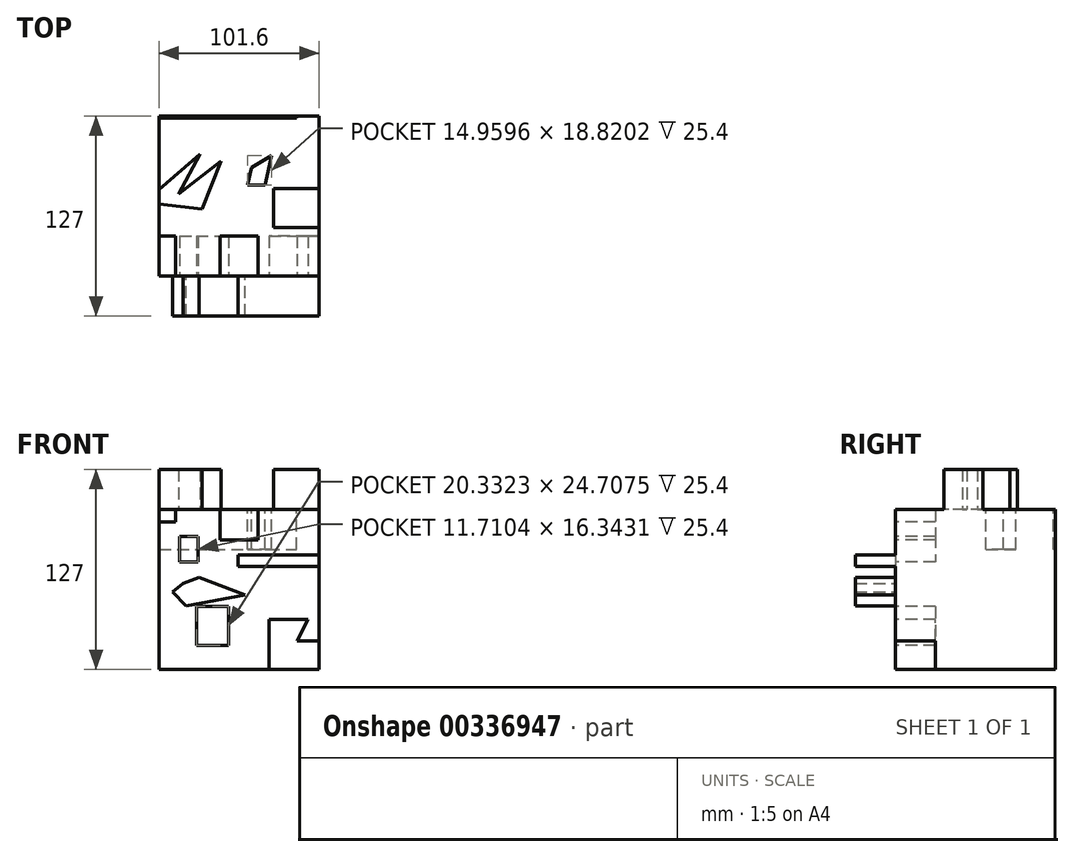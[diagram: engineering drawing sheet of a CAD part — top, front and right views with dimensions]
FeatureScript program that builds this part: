
annotation { "Feature Type Name" : "Feature", "Feature Type Description" : "" }
export const myFeature = defineFeature(function(context is Context, id is Id, definition is map)
    precondition{}
    {
        {
            var Q0;
            Q0=qCreatedBy(makeId("Front.planeOp"),FACE);
            var sketch = newSketch(context, id + "F0", { "sketchPlane" : qUnion([Q0])});
            skLineSegment(sketch, "E0.bottom", {"start": v(-49.93, 54.86) * mm, "end": v(51.67, 54.86) * mm});
            skLineSegment(sketch, "E0.top", {"start": v(-49.93, -46.74) * mm, "end": v(51.67, -46.74) * mm});
            skLineSegment(sketch, "E0.left", {"start": v(-49.93, 54.86) * mm, "end": v(-49.93, -46.74) * mm});
            skLineSegment(sketch, "E0.right", {"start": v(51.67, 54.86) * mm, "end": v(51.67, -46.74) * mm});
            skSolve(sketch);
        }
        {
            var Q0;
            Q0=makeQuery(id+"F0.imprint","IMPRINT",FACE,{"disambiguationData":[TD([[makeQuery(id+"F0.imprint","IMPRINT",EDGE,{"derivedFrom":sQuery(id+"F0.wireOp",EDGE,"E0.bottom")}),-1.0]])]});
            extrude(context, id + "F1", {"entities" : qUnion([Q0]), "oppositeDirection" : true, "depth" : 101.6 * mm});
        }
        {
            var Q0;
            Q0=makeQuery(id+"F1.opExtrude","CAP_FACE",FACE,{"disambiguationData":[OSD([sQuery(id+"F0.wireOp",EDGE,"E0.bottom"),sQuery(id+"F0.wireOp",EDGE,"E0.top"),sQuery(id+"F0.wireOp",EDGE,"E0.left"),sQuery(id+"F0.wireOp",EDGE,"E0.right")])],"isStart":true});
            var sketch = newSketch(context, id + "F2", { "sketchPlane" : qUnion([Q0])});
            skLineSegment(sketch, "E1.bottom", {"start": v(-49.93, 54.86) * mm, "end": v(-39.47, 54.86) * mm});
            skLineSegment(sketch, "E1.top", {"start": v(-49.93, 47.1) * mm, "end": v(-39.47, 47.1) * mm});
            skLineSegment(sketch, "E1.left", {"start": v(-49.93, 54.86) * mm, "end": v(-49.93, 47.1) * mm});
            skLineSegment(sketch, "E1.right", {"start": v(-39.47, 54.86) * mm, "end": v(-39.47, 47.1) * mm});
            skLineSegment(sketch, "E2.bottom", {"start": v(-36.77, 37.84) * mm, "end": v(-25.06, 37.84) * mm});
            skLineSegment(sketch, "E2.top", {"start": v(-36.77, 21.5) * mm, "end": v(-25.06, 21.5) * mm});
            skLineSegment(sketch, "E2.left", {"start": v(-36.77, 37.84) * mm, "end": v(-36.77, 21.5) * mm});
            skLineSegment(sketch, "E2.right", {"start": v(-25.06, 37.84) * mm, "end": v(-25.06, 21.5) * mm});
            skLineSegment(sketch, "E3", {"start": v(51.67, -28.57) * mm, "end": v(37.6, -28.57) * mm});
            skLineSegment(sketch, "E4", {"start": v(37.6, -28.57) * mm, "end": v(44.69, -14.92) * mm});
            skLineSegment(sketch, "E5", {"start": v(44.69, -14.92) * mm, "end": v(19.98, -14.92) * mm});
            skLineSegment(sketch, "E6", {"start": v(19.98, -14.92) * mm, "end": v(19.98, -46.74) * mm});
            skLineSegment(sketch, "E7", {"start": v(19.98, -46.74) * mm, "end": v(51.67, -46.74) * mm});
            skLineSegment(sketch, "E8", {"start": v(51.67, -46.74) * mm, "end": v(51.67, -28.57) * mm});
            skLineSegment(sketch, "E9.bottom", {"start": v(12.9, 54.86) * mm, "end": v(-11.3, 54.86) * mm});
            skLineSegment(sketch, "E9.top", {"start": v(12.9, 35.4) * mm, "end": v(-11.3, 35.4) * mm});
            skLineSegment(sketch, "E9.left", {"start": v(12.9, 54.86) * mm, "end": v(12.9, 35.4) * mm});
            skLineSegment(sketch, "E9.right", {"start": v(-11.3, 54.86) * mm, "end": v(-11.3, 35.4) * mm});
            skLineSegment(sketch, "E10.bottom", {"start": v(-26.22, -6.82) * mm, "end": v(-5.89, -6.82) * mm});
            skLineSegment(sketch, "E10.top", {"start": v(-26.22, -31.53) * mm, "end": v(-5.89, -31.53) * mm});
            skLineSegment(sketch, "E10.left", {"start": v(-26.22, -6.82) * mm, "end": v(-26.22, -31.53) * mm});
            skLineSegment(sketch, "E10.right", {"start": v(-5.89, -6.82) * mm, "end": v(-5.89, -31.53) * mm});
            skLineSegment(sketch, "E11.bottom", {"start": v(51.67, 26.13) * mm, "end": v(0.16, 26.13) * mm});
            skLineSegment(sketch, "E11.top", {"start": v(51.67, 18.53) * mm, "end": v(0.16, 18.53) * mm});
            skLineSegment(sketch, "E11.left", {"start": v(51.67, 26.13) * mm, "end": v(51.67, 18.53) * mm});
            skLineSegment(sketch, "E11.right", {"start": v(0.16, 26.13) * mm, "end": v(0.16, 18.53) * mm});
            skLineSegment(sketch, "E12", {"start": v(-34.84, 7.98) * mm, "end": v(-24.42, 11.84) * mm});
            skLineSegment(sketch, "E13", {"start": v(-24.42, 11.84) * mm, "end": v(4.8, 0.52) * mm});
            skLineSegment(sketch, "E14", {"start": v(4.8, 0.52) * mm, "end": v(-32.91, -6.43) * mm});
            skLineSegment(sketch, "E15", {"start": v(-32.91, -6.43) * mm, "end": v(-41.28, 2.45) * mm});
            skLineSegment(sketch, "E16", {"start": v(-41.28, 2.45) * mm, "end": v(-34.84, 7.98) * mm});
            skSolve(sketch);
        }
        {
            var Q0;
            Q0=makeQuery(id+"F2.imprint","IMPRINT",FACE,{"disambiguationData":[TD([[makeQuery(id+"F2.imprint","IMPRINT",EDGE,{"derivedFrom":sQuery(id+"F2.wireOp",EDGE,"E1.bottom")}),-1.0]])]});
            var Q1;
            Q1=makeQuery(id+"F2.imprint","IMPRINT",FACE,{"disambiguationData":[TD([[makeQuery(id+"F2.imprint","IMPRINT",EDGE,{"derivedFrom":sQuery(id+"F2.wireOp",EDGE,"E9.bottom")}),-1.0]])]});
            var Q2;
            Q2=makeQuery(id+"F2.imprint","IMPRINT",FACE,{"disambiguationData":[TD([[makeQuery(id+"F2.imprint","IMPRINT",EDGE,{"derivedFrom":sQuery(id+"F2.wireOp",EDGE,"E2.bottom")}),-1.0]])]});
            var Q3;
            Q3=makeQuery(id+"F2.imprint","IMPRINT",FACE,{"disambiguationData":[TD([[makeQuery(id+"F2.imprint","IMPRINT",EDGE,{"derivedFrom":sQuery(id+"F2.wireOp",EDGE,"E10.bottom")}),-1.0]])]});
            var Q4;
            Q4=makeQuery(id+"F2.imprint","IMPRINT",FACE,{"disambiguationData":[TD([[makeQuery(id+"F2.imprint","IMPRINT",EDGE,{"derivedFrom":sQuery(id+"F2.wireOp",EDGE,"E3")}),1.0]])]});
            extrude(context, id + "F3", {"entities" : qUnion([Q0, Q1, Q2, Q3, Q4]), "operationType" : NewBodyOperationType.REMOVE, "oppositeDirection" : true, "depth" : 25.4 * mm});
        }
        {
            var Q0;
            Q0=makeQuery(id+"F2.imprint","IMPRINT",FACE,{"disambiguationData":[TD([[makeQuery(id+"F2.imprint","IMPRINT",EDGE,{"derivedFrom":sQuery(id+"F2.wireOp",EDGE,"E12")}),-1.0]])]});
            var Q1;
            Q1=makeQuery(id+"F2.imprint","IMPRINT",FACE,{"disambiguationData":[TD([[makeQuery(id+"F2.imprint","IMPRINT",EDGE,{"derivedFrom":sQuery(id+"F2.wireOp",EDGE,"E11.bottom")}),1.0]])]});
            extrude(context, id + "F4", {"entities" : qUnion([Q0, Q1]), "operationType" : NewBodyOperationType.ADD, "depth" : 25.4 * mm});
        }
        {
            var Q0;
            Q0=makeQuery(id+"F1.opExtrude","SWEPT_FACE",FACE,{"disambiguationData":[OSD([sQuery(id+"F0.wireOp",EDGE,"E0.bottom")])]});
            var sketch = newSketch(context, id + "F5", { "sketchPlane" : qUnion([Q0])});
            skLineSegment(sketch, "E17.bottom", {"start": v(51.67, 55.55) * mm, "end": v(22.83, 55.55) * mm});
            skLineSegment(sketch, "E17.top", {"start": v(51.67, 30.78) * mm, "end": v(22.83, 30.78) * mm});
            skLineSegment(sketch, "E17.left", {"start": v(51.67, 55.55) * mm, "end": v(51.67, 30.78) * mm});
            skLineSegment(sketch, "E17.right", {"start": v(22.83, 55.55) * mm, "end": v(22.83, 30.78) * mm});
            skLineSegment(sketch, "E18.bottom", {"start": v(-49.93, 100.43) * mm, "end": v(37.3, 100.43) * mm});
            skLineSegment(sketch, "E18.top", {"start": v(-49.93, 101.6) * mm, "end": v(37.3, 101.6) * mm});
            skLineSegment(sketch, "E18.left", {"start": v(-49.93, 100.43) * mm, "end": v(-49.93, 101.6) * mm});
            skLineSegment(sketch, "E18.right", {"start": v(37.3, 100.43) * mm, "end": v(37.3, 101.6) * mm});
            skLineSegment(sketch, "E19", {"start": v(-49.93, 55.06) * mm, "end": v(-23.98, 77.42) * mm});
            skLineSegment(sketch, "E20", {"start": v(-23.98, 77.42) * mm, "end": v(-37.5, 52.17) * mm});
            skLineSegment(sketch, "E21", {"start": v(-37.5, 52.17) * mm, "end": v(-10.47, 72.92) * mm});
            skLineSegment(sketch, "E22", {"start": v(-10.47, 72.92) * mm, "end": v(-22.54, 42.68) * mm});
            skLineSegment(sketch, "E23", {"start": v(-22.54, 42.68) * mm, "end": v(-49.93, 45.57) * mm});
            skLineSegment(sketch, "E24", {"start": v(-49.93, 45.57) * mm, "end": v(-49.93, 55.06) * mm});
            skLineSegment(sketch, "E25", {"start": v(21.38, 76.46) * mm, "end": v(8.83, 68.74) * mm});
            skLineSegment(sketch, "E26", {"start": v(8.83, 68.74) * mm, "end": v(6.42, 57.64) * mm});
            skLineSegment(sketch, "E27", {"start": v(6.42, 57.64) * mm, "end": v(17.36, 57.64) * mm});
            skLineSegment(sketch, "E28", {"start": v(17.36, 57.64) * mm, "end": v(21.38, 76.46) * mm});
            skSolve(sketch);
        }
        {
            var Q0;
            Q0=makeQuery(id+"F5.imprint","IMPRINT",FACE,{"disambiguationData":[TD([[makeQuery(id+"F5.imprint","IMPRINT",EDGE,{"derivedFrom":sQuery(id+"F5.wireOp",EDGE,"E17.bottom")}),1.0]])]});
            var Q1;
            Q1=makeQuery(id+"F5.imprint","IMPRINT",FACE,{"disambiguationData":[TD([[makeQuery(id+"F5.imprint","IMPRINT",EDGE,{"derivedFrom":sQuery(id+"F5.wireOp",EDGE,"E19")}),-1.0]])]});
            extrude(context, id + "F6", {"entities" : qUnion([Q0, Q1]), "operationType" : NewBodyOperationType.ADD, "depth" : 25.4 * mm});
        }
        {
            var Q0;
            Q0=makeQuery(id+"F5.imprint","IMPRINT",FACE,{"disambiguationData":[TD([[makeQuery(id+"F5.imprint","IMPRINT",EDGE,{"derivedFrom":sQuery(id+"F5.wireOp",EDGE,"E18.bottom")}),1.0]])]});
            var Q1;
            Q1=makeQuery(id+"F5.imprint","IMPRINT",FACE,{"disambiguationData":[TD([[makeQuery(id+"F5.imprint","IMPRINT",EDGE,{"derivedFrom":sQuery(id+"F5.wireOp",EDGE,"E25")}),1.0]])]});
            extrude(context, id + "F7", {"entities" : qUnion([Q0, Q1]), "operationType" : NewBodyOperationType.REMOVE, "oppositeDirection" : true, "depth" : 25.4 * mm});
        }
    });
